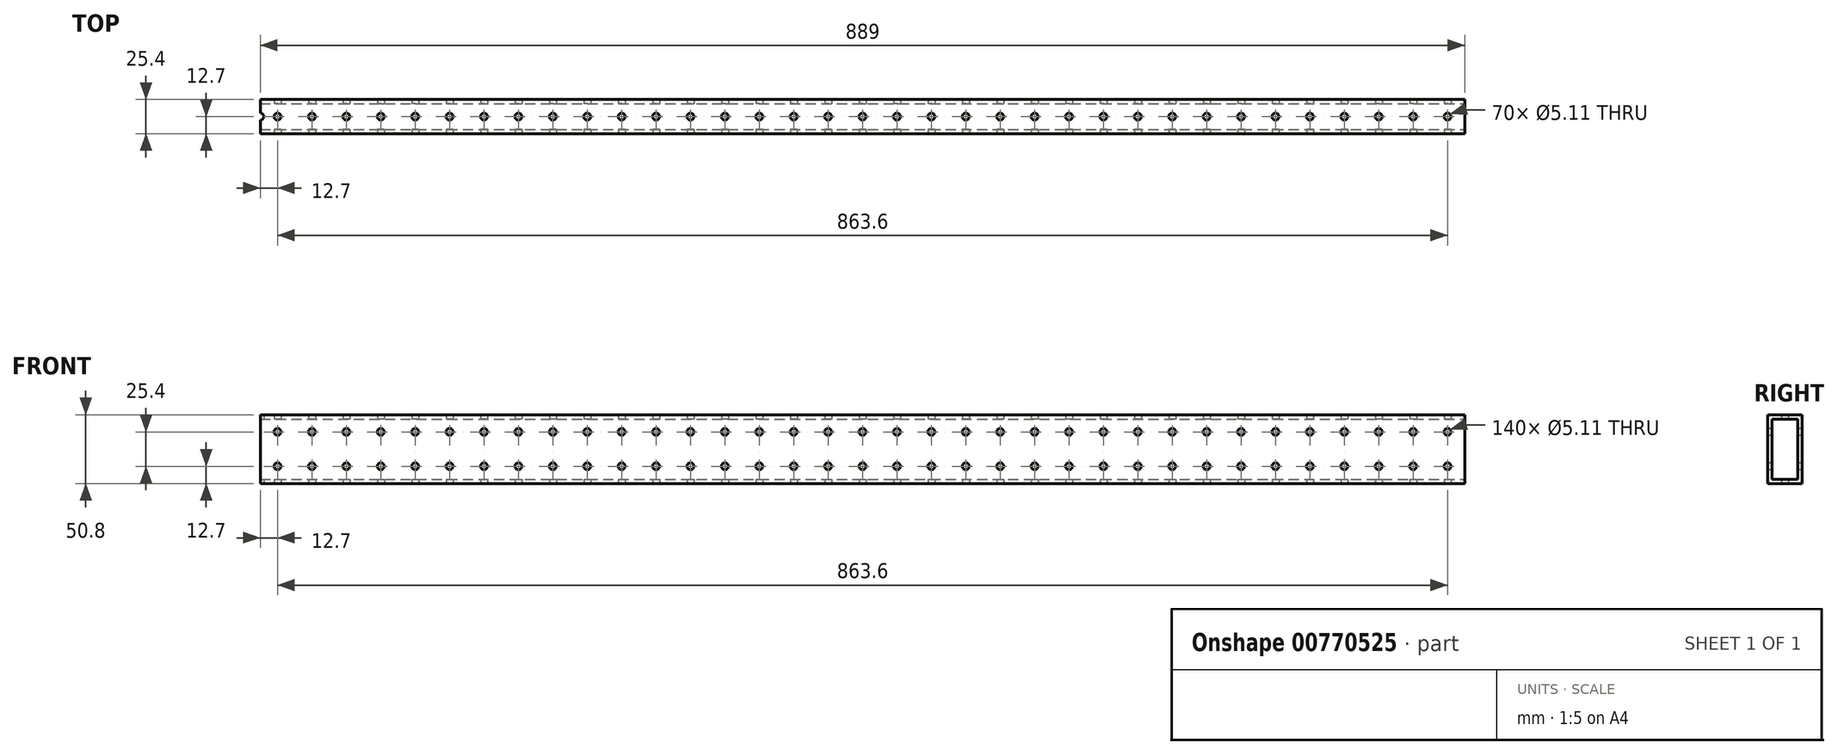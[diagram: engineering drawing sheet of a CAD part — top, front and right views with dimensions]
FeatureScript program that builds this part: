
annotation { "Feature Type Name" : "Feature", "Feature Type Description" : "" }
export const myFeature = defineFeature(function(context is Context, id is Id, definition is map)
    precondition{}
    {
        {
            var Q0;
            Q0=qCreatedBy(makeId("Front.planeOp"),FACE);
            var sketch = newSketch(context, id + "F0", { "sketchPlane" : qUnion([Q0])});
            skLineSegment(sketch, "E0.bottom", {"start": v(444.5, -25.4) * mm, "end": v(-444.5, -25.4) * mm});
            skLineSegment(sketch, "E0.top", {"start": v(444.5, 25.4) * mm, "end": v(-444.5, 25.4) * mm});
            skLineSegment(sketch, "E0.left", {"start": v(444.5, -25.4) * mm, "end": v(444.5, 25.4) * mm});
            skLineSegment(sketch, "E0.right", {"start": v(-444.5, -25.4) * mm, "end": v(-444.5, 25.4) * mm});
            skPoint(sketch, "E0.middle", {"position": v(0, 0) * mm});
            skSolve(sketch);
        }
        {
            var Q0;
            Q0=makeQuery(id+"F0.imprint","IMPRINT",FACE,{"disambiguationData":[TD([[makeQuery(id+"F0.imprint","IMPRINT",EDGE,{"derivedFrom":sQuery(id+"F0.wireOp",EDGE,"E0.bottom")}),-1.0]])]});
            extrude(context, id + "F1", {"entities" : qUnion([Q0]), "depth" : 25.4 * mm, "offsetDistance" : 25.4 * mm});
        }
        {
            var Q0;
            Q0=makeQuery(id+"F1.opExtrude","CAP_FACE",FACE,{"disambiguationData":[OSD([sQuery(id+"F0.wireOp",EDGE,"E0.bottom"),sQuery(id+"F0.wireOp",EDGE,"E0.top"),sQuery(id+"F0.wireOp",EDGE,"E0.left"),sQuery(id+"F0.wireOp",EDGE,"E0.right")])],"isStart":false});
            var sketch = newSketch(context, id + "F2", { "sketchPlane" : qUnion([Q0])});
            skCircle(sketch, "E1", {"center": v(-431.8, -12.7) * mm, "radius": 2.55 * mm});
            skCircle(sketch, "E2.0.1.0", {"center": v(-431.8, 12.7) * mm, "radius": 2.55 * mm});
            skCircle(sketch, "E2.1.0.0", {"center": v(-406.4, -12.7) * mm, "radius": 2.55 * mm});
            skCircle(sketch, "E2.1.1.0", {"center": v(-406.4, 12.7) * mm, "radius": 2.55 * mm});
            skCircle(sketch, "E2.2.0.0", {"center": v(-381, -12.7) * mm, "radius": 2.55 * mm});
            skCircle(sketch, "E2.2.1.0", {"center": v(-381, 12.7) * mm, "radius": 2.55 * mm});
            skCircle(sketch, "E2.3.0.0", {"center": v(-355.6, -12.7) * mm, "radius": 2.55 * mm});
            skCircle(sketch, "E2.3.1.0", {"center": v(-355.6, 12.7) * mm, "radius": 2.55 * mm});
            skCircle(sketch, "E2.4.0.0", {"center": v(-330.2, -12.7) * mm, "radius": 2.55 * mm});
            skCircle(sketch, "E2.4.1.0", {"center": v(-330.2, 12.7) * mm, "radius": 2.55 * mm});
            skCircle(sketch, "E2.5.0.0", {"center": v(-304.8, -12.7) * mm, "radius": 2.55 * mm});
            skCircle(sketch, "E2.5.1.0", {"center": v(-304.8, 12.7) * mm, "radius": 2.55 * mm});
            skCircle(sketch, "E2.6.0.0", {"center": v(-279.4, -12.7) * mm, "radius": 2.55 * mm});
            skCircle(sketch, "E2.6.1.0", {"center": v(-279.4, 12.7) * mm, "radius": 2.55 * mm});
            skCircle(sketch, "E2.7.0.0", {"center": v(-254, -12.7) * mm, "radius": 2.55 * mm});
            skCircle(sketch, "E2.7.1.0", {"center": v(-254, 12.7) * mm, "radius": 2.55 * mm});
            skCircle(sketch, "E2.8.0.0", {"center": v(-228.6, -12.7) * mm, "radius": 2.55 * mm});
            skCircle(sketch, "E2.8.1.0", {"center": v(-228.6, 12.7) * mm, "radius": 2.55 * mm});
            skCircle(sketch, "E2.9.0.0", {"center": v(-203.2, -12.7) * mm, "radius": 2.55 * mm});
            skCircle(sketch, "E2.9.1.0", {"center": v(-203.2, 12.7) * mm, "radius": 2.55 * mm});
            skCircle(sketch, "E2.10.0.0", {"center": v(-177.8, -12.7) * mm, "radius": 2.55 * mm});
            skCircle(sketch, "E2.10.1.0", {"center": v(-177.8, 12.7) * mm, "radius": 2.55 * mm});
            skCircle(sketch, "E2.11.0.0", {"center": v(-152.4, -12.7) * mm, "radius": 2.55 * mm});
            skCircle(sketch, "E2.11.1.0", {"center": v(-152.4, 12.7) * mm, "radius": 2.55 * mm});
            skCircle(sketch, "E2.12.0.0", {"center": v(-127, -12.7) * mm, "radius": 2.55 * mm});
            skCircle(sketch, "E2.12.1.0", {"center": v(-127, 12.7) * mm, "radius": 2.55 * mm});
            skCircle(sketch, "E2.13.0.0", {"center": v(-101.6, -12.7) * mm, "radius": 2.55 * mm});
            skCircle(sketch, "E2.13.1.0", {"center": v(-101.6, 12.7) * mm, "radius": 2.55 * mm});
            skCircle(sketch, "E2.14.0.0", {"center": v(-76.2, -12.7) * mm, "radius": 2.55 * mm});
            skCircle(sketch, "E2.14.1.0", {"center": v(-76.2, 12.7) * mm, "radius": 2.55 * mm});
            skCircle(sketch, "E2.15.0.0", {"center": v(-50.8, -12.7) * mm, "radius": 2.55 * mm});
            skCircle(sketch, "E2.15.1.0", {"center": v(-50.8, 12.7) * mm, "radius": 2.55 * mm});
            skCircle(sketch, "E2.16.0.0", {"center": v(-25.4, -12.7) * mm, "radius": 2.55 * mm});
            skCircle(sketch, "E2.16.1.0", {"center": v(-25.4, 12.7) * mm, "radius": 2.55 * mm});
            skCircle(sketch, "E2.17.0.0", {"center": v(0, -12.7) * mm, "radius": 2.55 * mm});
            skCircle(sketch, "E2.17.1.0", {"center": v(0, 12.7) * mm, "radius": 2.55 * mm});
            skCircle(sketch, "E2.18.0.0", {"center": v(25.4, -12.7) * mm, "radius": 2.55 * mm});
            skCircle(sketch, "E2.18.1.0", {"center": v(25.4, 12.7) * mm, "radius": 2.55 * mm});
            skCircle(sketch, "E2.19.0.0", {"center": v(50.8, -12.7) * mm, "radius": 2.55 * mm});
            skCircle(sketch, "E2.19.1.0", {"center": v(50.8, 12.7) * mm, "radius": 2.55 * mm});
            skCircle(sketch, "E2.20.0.0", {"center": v(76.2, -12.7) * mm, "radius": 2.55 * mm});
            skCircle(sketch, "E2.20.1.0", {"center": v(76.2, 12.7) * mm, "radius": 2.55 * mm});
            skCircle(sketch, "E2.21.0.0", {"center": v(101.6, -12.7) * mm, "radius": 2.55 * mm});
            skCircle(sketch, "E2.21.1.0", {"center": v(101.6, 12.7) * mm, "radius": 2.55 * mm});
            skCircle(sketch, "E2.22.0.0", {"center": v(127, -12.7) * mm, "radius": 2.55 * mm});
            skCircle(sketch, "E2.22.1.0", {"center": v(127, 12.7) * mm, "radius": 2.55 * mm});
            skCircle(sketch, "E2.23.0.0", {"center": v(152.4, -12.7) * mm, "radius": 2.55 * mm});
            skCircle(sketch, "E2.23.1.0", {"center": v(152.4, 12.7) * mm, "radius": 2.55 * mm});
            skCircle(sketch, "E2.24.0.0", {"center": v(177.8, -12.7) * mm, "radius": 2.55 * mm});
            skCircle(sketch, "E2.24.1.0", {"center": v(177.8, 12.7) * mm, "radius": 2.55 * mm});
            skCircle(sketch, "E2.25.0.0", {"center": v(203.2, -12.7) * mm, "radius": 2.55 * mm});
            skCircle(sketch, "E2.25.1.0", {"center": v(203.2, 12.7) * mm, "radius": 2.55 * mm});
            skCircle(sketch, "E2.26.0.0", {"center": v(228.6, -12.7) * mm, "radius": 2.55 * mm});
            skCircle(sketch, "E2.26.1.0", {"center": v(228.6, 12.7) * mm, "radius": 2.55 * mm});
            skCircle(sketch, "E2.27.0.0", {"center": v(254, -12.7) * mm, "radius": 2.55 * mm});
            skCircle(sketch, "E2.27.1.0", {"center": v(254, 12.7) * mm, "radius": 2.55 * mm});
            skCircle(sketch, "E2.28.0.0", {"center": v(279.4, -12.7) * mm, "radius": 2.55 * mm});
            skCircle(sketch, "E2.28.1.0", {"center": v(279.4, 12.7) * mm, "radius": 2.55 * mm});
            skCircle(sketch, "E2.29.0.0", {"center": v(304.8, -12.7) * mm, "radius": 2.55 * mm});
            skCircle(sketch, "E2.29.1.0", {"center": v(304.8, 12.7) * mm, "radius": 2.55 * mm});
            skCircle(sketch, "E2.30.0.0", {"center": v(330.2, -12.7) * mm, "radius": 2.55 * mm});
            skCircle(sketch, "E2.30.1.0", {"center": v(330.2, 12.7) * mm, "radius": 2.55 * mm});
            skCircle(sketch, "E2.31.0.0", {"center": v(355.6, -12.7) * mm, "radius": 2.55 * mm});
            skCircle(sketch, "E2.31.1.0", {"center": v(355.6, 12.7) * mm, "radius": 2.55 * mm});
            skCircle(sketch, "E2.32.0.0", {"center": v(381, -12.7) * mm, "radius": 2.55 * mm});
            skCircle(sketch, "E2.32.1.0", {"center": v(381, 12.7) * mm, "radius": 2.55 * mm});
            skCircle(sketch, "E2.33.0.0", {"center": v(406.4, -12.7) * mm, "radius": 2.55 * mm});
            skCircle(sketch, "E2.33.1.0", {"center": v(406.4, 12.7) * mm, "radius": 2.55 * mm});
            skCircle(sketch, "E2.34.0.0", {"center": v(431.8, -12.7) * mm, "radius": 2.55 * mm});
            skCircle(sketch, "E2.34.1.0", {"center": v(431.8, 12.7) * mm, "radius": 2.55 * mm});
            skLineSegment(sketch, "E2.direction1", {"start": v(-431.8, -12.7) * mm, "end": v(-406.4, -12.7) * mm, "construction": true});
            skLineSegment(sketch, "E2.direction2", {"start": v(-431.8, -12.7) * mm, "end": v(-431.8, 12.7) * mm, "construction": true});
            skSolve(sketch);
        }
        {
            var Q0;
            Q0=sQuery(id+"F2.wireOp",VERTEX,"E2.30.0.0.center");
            var Q1;
            Q1=sQuery(id+"F2.wireOp",VERTEX,"E2.14.0.0.center");
            var Q2;
            Q2=sQuery(id+"F2.wireOp",VERTEX,"E2.22.0.0.center");
            var Q3;
            Q3=sQuery(id+"F2.wireOp",VERTEX,"E2.25.1.0.center");
            var Q4;
            Q4=sQuery(id+"F2.wireOp",VERTEX,"E2.17.1.0.center");
            var Q5;
            Q5=sQuery(id+"F2.wireOp",VERTEX,"E2.9.1.0.center");
            var Q6;
            Q6=sQuery(id+"F2.wireOp",VERTEX,"E2.6.1.0.center");
            var Q7;
            Q7=sQuery(id+"F2.wireOp",VERTEX,"E2.30.1.0.center");
            var Q8;
            Q8=sQuery(id+"F2.wireOp",VERTEX,"E2.22.1.0.center");
            var Q9;
            Q9=sQuery(id+"F2.wireOp",VERTEX,"E2.14.1.0.center");
            var Q10;
            Q10=sQuery(id+"F2.wireOp",VERTEX,"E2.26.0.0.center");
            var Q11;
            Q11=sQuery(id+"F2.wireOp",VERTEX,"E2.18.0.0.center");
            var Q12;
            Q12=sQuery(id+"F2.wireOp",VERTEX,"E2.10.0.0.center");
            var Q13;
            Q13=sQuery(id+"F2.wireOp",VERTEX,"E2.34.0.0.center");
            var Q14;
            Q14=sQuery(id+"F2.wireOp",VERTEX,"E2.4.1.0.center");
            var Q15;
            Q15=sQuery(id+"F2.wireOp",VERTEX,"E2.7.0.0.center");
            var Q16;
            Q16=sQuery(id+"F2.wireOp",VERTEX,"E2.5.0.0.center");
            var Q17;
            Q17=sQuery(id+"F2.wireOp",VERTEX,"E2.5.1.0.center");
            var Q18;
            Q18=sQuery(id+"F2.wireOp",VERTEX,"E2.31.0.0.center");
            var Q19;
            Q19=sQuery(id+"F2.wireOp",VERTEX,"E2.23.0.0.center");
            var Q20;
            Q20=sQuery(id+"F2.wireOp",VERTEX,"E2.15.0.0.center");
            var Q21;
            Q21=sQuery(id+"F2.wireOp",VERTEX,"E1.center");
            var Q22;
            Q22=sQuery(id+"F2.wireOp",VERTEX,"E2.0.1.0.center");
            var Q23;
            Q23=sQuery(id+"F2.wireOp",VERTEX,"E2.1.0.0.center");
            var Q24;
            Q24=sQuery(id+"F2.wireOp",VERTEX,"E2.1.1.0.center");
            var Q25;
            Q25=sQuery(id+"F2.wireOp",VERTEX,"E2.2.0.0.center");
            var Q26;
            Q26=sQuery(id+"F2.wireOp",VERTEX,"E2.2.1.0.center");
            var Q27;
            Q27=sQuery(id+"F2.wireOp",VERTEX,"E2.3.0.0.center");
            var Q28;
            Q28=sQuery(id+"F2.wireOp",VERTEX,"E2.3.1.0.center");
            var Q29;
            Q29=sQuery(id+"F2.wireOp",VERTEX,"E2.4.0.0.center");
            var Q30;
            Q30=sQuery(id+"F2.wireOp",VERTEX,"E2.26.1.0.center");
            var Q31;
            Q31=sQuery(id+"F2.wireOp",VERTEX,"E2.18.1.0.center");
            var Q32;
            Q32=sQuery(id+"F2.wireOp",VERTEX,"E2.10.1.0.center");
            var Q33;
            Q33=sQuery(id+"F2.wireOp",VERTEX,"E2.33.1.0.center");
            var Q34;
            Q34=sQuery(id+"F2.wireOp",VERTEX,"E2.6.0.0.center");
            var Q35;
            Q35=sQuery(id+"F2.wireOp",VERTEX,"E2.13.1.0.center");
            var Q36;
            Q36=sQuery(id+"F2.wireOp",VERTEX,"E2.21.1.0.center");
            var Q37;
            Q37=sQuery(id+"F2.wireOp",VERTEX,"E2.25.0.0.center");
            var Q38;
            Q38=sQuery(id+"F2.wireOp",VERTEX,"E2.17.0.0.center");
            var Q39;
            Q39=sQuery(id+"F2.wireOp",VERTEX,"E2.33.0.0.center");
            var Q40;
            Q40=sQuery(id+"F2.wireOp",VERTEX,"E2.29.1.0.center");
            var Q41;
            Q41=sQuery(id+"F2.wireOp",VERTEX,"E2.9.0.0.center");
            var Q42;
            Q42=sQuery(id+"F2.wireOp",VERTEX,"E2.12.0.0.center");
            var Q43;
            Q43=sQuery(id+"F2.wireOp",VERTEX,"E2.20.0.0.center");
            var Q44;
            Q44=sQuery(id+"F2.wireOp",VERTEX,"E2.28.0.0.center");
            var Q45;
            Q45=sQuery(id+"F2.wireOp",VERTEX,"E2.16.1.0.center");
            var Q46;
            Q46=sQuery(id+"F2.wireOp",VERTEX,"E2.13.0.0.center");
            var Q47;
            Q47=sQuery(id+"F2.wireOp",VERTEX,"E2.24.1.0.center");
            var Q48;
            Q48=sQuery(id+"F2.wireOp",VERTEX,"E2.21.0.0.center");
            var Q49;
            Q49=sQuery(id+"F2.wireOp",VERTEX,"E2.29.0.0.center");
            var Q50;
            Q50=sQuery(id+"F2.wireOp",VERTEX,"E2.32.1.0.center");
            var Q51;
            Q51=sQuery(id+"F2.wireOp",VERTEX,"E2.8.1.0.center");
            var Q52;
            Q52=sQuery(id+"F2.wireOp",VERTEX,"E2.11.1.0.center");
            var Q53;
            Q53=sQuery(id+"F2.wireOp",VERTEX,"E2.19.1.0.center");
            var Q54;
            Q54=sQuery(id+"F2.wireOp",VERTEX,"E2.27.1.0.center");
            var Q55;
            Q55=sQuery(id+"F2.wireOp",VERTEX,"E2.34.1.0.center");
            var Q56;
            Q56=sQuery(id+"F2.wireOp",VERTEX,"E2.7.1.0.center");
            var Q57;
            Q57=sQuery(id+"F2.wireOp",VERTEX,"E2.31.1.0.center");
            var Q58;
            Q58=sQuery(id+"F2.wireOp",VERTEX,"E2.23.1.0.center");
            var Q59;
            Q59=sQuery(id+"F2.wireOp",VERTEX,"E2.15.1.0.center");
            var Q60;
            Q60=sQuery(id+"F2.wireOp",VERTEX,"E2.27.0.0.center");
            var Q61;
            Q61=sQuery(id+"F2.wireOp",VERTEX,"E2.19.0.0.center");
            var Q62;
            Q62=sQuery(id+"F2.wireOp",VERTEX,"E2.11.0.0.center");
            var Q63;
            Q63=sQuery(id+"F2.wireOp",VERTEX,"E2.8.0.0.center");
            var Q64;
            Q64=sQuery(id+"F2.wireOp",VERTEX,"E2.28.1.0.center");
            var Q65;
            Q65=sQuery(id+"F2.wireOp",VERTEX,"E2.32.0.0.center");
            var Q66;
            Q66=sQuery(id+"F2.wireOp",VERTEX,"E2.20.1.0.center");
            var Q67;
            Q67=sQuery(id+"F2.wireOp",VERTEX,"E2.24.0.0.center");
            var Q68;
            Q68=sQuery(id+"F2.wireOp",VERTEX,"E2.12.1.0.center");
            var Q69;
            Q69=sQuery(id+"F2.wireOp",VERTEX,"E2.16.0.0.center");
            var Q70;
            Q70=makeQuery(id+"F1.opExtrude","SWEPT_BODY",BODY,{"disambiguationData":[OSD([sQuery(id+"F0.wireOp",EDGE,"E0.bottom"),sQuery(id+"F0.wireOp",EDGE,"E0.top"),sQuery(id+"F0.wireOp",EDGE,"E0.left"),sQuery(id+"F0.wireOp",EDGE,"E0.right")])]});
            hole(context, id + "F3", {"style" : HoleStyle.SIMPLE, "endStyle" : HoleEndStyle.BLIND, "holeDiameter" : 5.1 * mm, "majorDiameter" : 6.35 * mm, "holeDepth" : 50.8 * mm, "isTappedThrough" : true, "tappedDepth" : 12.7 * mm, "tapClearance" : 3, "startFromSketch" : true, "locations" : qUnion([Q0, Q1, Q2, Q3, Q4, Q5, Q6, Q7, Q8, Q9, Q10, Q11, Q12, Q13, Q14, Q15, Q16, Q17, Q18, Q19, Q20, Q21, Q22, Q23, Q24, Q25, Q26, Q27, Q28, Q29, Q30, Q31, Q32, Q33, Q34, Q35, Q36, Q37, Q38, Q39, Q40, Q41, Q42, Q43, Q44, Q45, Q46, Q47, Q48, Q49, Q50, Q51, Q52, Q53, Q54, Q55, Q56, Q57, Q58, Q59, Q60, Q61, Q62, Q63, Q64, Q65, Q66, Q67, Q68, Q69]), "scope" : qUnion([Q70])});
        }
        {
            var Q0;
            Q0=makeQuery(id+"F1.opExtrude","SWEPT_FACE",FACE,{"disambiguationData":[OSD([sQuery(id+"F0.wireOp",EDGE,"E0.bottom")])]});
            var sketch = newSketch(context, id + "F4", { "sketchPlane" : qUnion([Q0])});
            skCircle(sketch, "E3", {"center": v(-431.8, 12.7) * mm, "radius": 2.55 * mm});
            skPoint(sketch, "E3.centerSnap0", {"position": v(-444.5, 12.7) * mm});
            skCircle(sketch, "E4.1.0.0", {"center": v(-406.4, 12.7) * mm, "radius": 2.55 * mm});
            skCircle(sketch, "E4.2.0.0", {"center": v(-381, 12.7) * mm, "radius": 2.55 * mm});
            skCircle(sketch, "E4.3.0.0", {"center": v(-355.6, 12.7) * mm, "radius": 2.55 * mm});
            skCircle(sketch, "E4.4.0.0", {"center": v(-330.2, 12.7) * mm, "radius": 2.55 * mm});
            skCircle(sketch, "E4.5.0.0", {"center": v(-304.8, 12.7) * mm, "radius": 2.55 * mm});
            skCircle(sketch, "E4.6.0.0", {"center": v(-279.4, 12.7) * mm, "radius": 2.55 * mm});
            skCircle(sketch, "E4.7.0.0", {"center": v(-254, 12.7) * mm, "radius": 2.55 * mm});
            skCircle(sketch, "E4.8.0.0", {"center": v(-228.6, 12.7) * mm, "radius": 2.55 * mm});
            skCircle(sketch, "E4.9.0.0", {"center": v(-203.2, 12.7) * mm, "radius": 2.55 * mm});
            skCircle(sketch, "E4.10.0.0", {"center": v(-177.8, 12.7) * mm, "radius": 2.55 * mm});
            skCircle(sketch, "E4.11.0.0", {"center": v(-152.4, 12.7) * mm, "radius": 2.55 * mm});
            skCircle(sketch, "E4.12.0.0", {"center": v(-127, 12.7) * mm, "radius": 2.55 * mm});
            skCircle(sketch, "E4.13.0.0", {"center": v(-101.6, 12.7) * mm, "radius": 2.55 * mm});
            skCircle(sketch, "E4.14.0.0", {"center": v(-76.2, 12.7) * mm, "radius": 2.55 * mm});
            skCircle(sketch, "E4.15.0.0", {"center": v(-50.8, 12.7) * mm, "radius": 2.55 * mm});
            skCircle(sketch, "E4.16.0.0", {"center": v(-25.4, 12.7) * mm, "radius": 2.55 * mm});
            skCircle(sketch, "E4.17.0.0", {"center": v(0, 12.7) * mm, "radius": 2.55 * mm});
            skCircle(sketch, "E4.18.0.0", {"center": v(25.4, 12.7) * mm, "radius": 2.55 * mm});
            skCircle(sketch, "E4.19.0.0", {"center": v(50.8, 12.7) * mm, "radius": 2.55 * mm});
            skCircle(sketch, "E4.20.0.0", {"center": v(76.2, 12.7) * mm, "radius": 2.55 * mm});
            skCircle(sketch, "E4.21.0.0", {"center": v(101.6, 12.7) * mm, "radius": 2.55 * mm});
            skCircle(sketch, "E4.22.0.0", {"center": v(127, 12.7) * mm, "radius": 2.55 * mm});
            skCircle(sketch, "E4.23.0.0", {"center": v(152.4, 12.7) * mm, "radius": 2.55 * mm});
            skCircle(sketch, "E4.24.0.0", {"center": v(177.8, 12.7) * mm, "radius": 2.55 * mm});
            skCircle(sketch, "E4.25.0.0", {"center": v(203.2, 12.7) * mm, "radius": 2.55 * mm});
            skCircle(sketch, "E4.26.0.0", {"center": v(228.6, 12.7) * mm, "radius": 2.55 * mm});
            skCircle(sketch, "E4.27.0.0", {"center": v(254, 12.7) * mm, "radius": 2.55 * mm});
            skCircle(sketch, "E4.28.0.0", {"center": v(279.4, 12.7) * mm, "radius": 2.55 * mm});
            skCircle(sketch, "E4.29.0.0", {"center": v(304.8, 12.7) * mm, "radius": 2.55 * mm});
            skCircle(sketch, "E4.30.0.0", {"center": v(330.2, 12.7) * mm, "radius": 2.55 * mm});
            skCircle(sketch, "E4.31.0.0", {"center": v(355.6, 12.7) * mm, "radius": 2.55 * mm});
            skCircle(sketch, "E4.32.0.0", {"center": v(381, 12.7) * mm, "radius": 2.55 * mm});
            skCircle(sketch, "E4.33.0.0", {"center": v(406.4, 12.7) * mm, "radius": 2.55 * mm});
            skCircle(sketch, "E4.34.0.0", {"center": v(431.8, 12.7) * mm, "radius": 2.55 * mm});
            skLineSegment(sketch, "E4.direction1", {"start": v(-431.8, 12.7) * mm, "end": v(-406.4, 12.7) * mm, "construction": true});
            skSolve(sketch);
        }
        {
            var Q0;
            Q0=sQuery(id+"F4.wireOp",VERTEX,"E4.26.0.0.center");
            var Q1;
            Q1=sQuery(id+"F4.wireOp",VERTEX,"E4.7.0.0.center");
            var Q2;
            Q2=sQuery(id+"F4.wireOp",VERTEX,"E4.33.0.0.center");
            var Q3;
            Q3=sQuery(id+"F4.wireOp",VERTEX,"E4.17.0.0.center");
            var Q4;
            Q4=sQuery(id+"F4.wireOp",VERTEX,"E4.6.0.0.center");
            var Q5;
            Q5=sQuery(id+"F4.wireOp",VERTEX,"E4.9.0.0.center");
            var Q6;
            Q6=sQuery(id+"F4.wireOp",VERTEX,"E4.29.0.0.center");
            var Q7;
            Q7=sQuery(id+"F4.wireOp",VERTEX,"E4.8.0.0.center");
            var Q8;
            Q8=sQuery(id+"F4.wireOp",VERTEX,"E4.13.0.0.center");
            var Q9;
            Q9=sQuery(id+"F4.wireOp",VERTEX,"E4.24.0.0.center");
            var Q10;
            Q10=sQuery(id+"F4.wireOp",VERTEX,"E4.16.0.0.center");
            var Q11;
            Q11=sQuery(id+"F4.wireOp",VERTEX,"E4.32.0.0.center");
            var Q12;
            Q12=sQuery(id+"F4.wireOp",VERTEX,"E4.23.0.0.center");
            var Q13;
            Q13=sQuery(id+"F4.wireOp",VERTEX,"E4.22.0.0.center");
            var Q14;
            Q14=sQuery(id+"F4.wireOp",VERTEX,"E4.28.0.0.center");
            var Q15;
            Q15=sQuery(id+"F4.wireOp",VERTEX,"E4.19.0.0.center");
            var Q16;
            Q16=sQuery(id+"F4.wireOp",VERTEX,"E4.31.0.0.center");
            var Q17;
            Q17=sQuery(id+"F4.wireOp",VERTEX,"E4.15.0.0.center");
            var Q18;
            Q18=sQuery(id+"F4.wireOp",VERTEX,"E4.21.0.0.center");
            var Q19;
            Q19=sQuery(id+"F4.wireOp",VERTEX,"E4.18.0.0.center");
            var Q20;
            Q20=sQuery(id+"F4.wireOp",VERTEX,"E4.34.0.0.center");
            var Q21;
            Q21=sQuery(id+"F4.wireOp",VERTEX,"E4.27.0.0.center");
            var Q22;
            Q22=sQuery(id+"F4.wireOp",VERTEX,"E4.14.0.0.center");
            var Q23;
            Q23=sQuery(id+"F4.wireOp",VERTEX,"E4.30.0.0.center");
            var Q24;
            Q24=sQuery(id+"F4.wireOp",VERTEX,"E4.25.0.0.center");
            var Q25;
            Q25=sQuery(id+"F4.wireOp",VERTEX,"E3.centerSnap0");
            var Q26;
            Q26=sQuery(id+"F4.wireOp",VERTEX,"E4.direction1.start");
            var Q27;
            Q27=sQuery(id+"F4.wireOp",VERTEX,"E4.2.0.0.center");
            var Q28;
            Q28=sQuery(id+"F4.wireOp",VERTEX,"E4.20.0.0.center");
            var Q29;
            Q29=sQuery(id+"F4.wireOp",VERTEX,"E4.3.0.0.center");
            var Q30;
            Q30=sQuery(id+"F4.wireOp",VERTEX,"E4.5.0.0.center");
            var Q31;
            Q31=sQuery(id+"F4.wireOp",VERTEX,"E4.4.0.0.center");
            var Q32;
            Q32=sQuery(id+"F4.wireOp",VERTEX,"E4.10.0.0.center");
            var Q33;
            Q33=sQuery(id+"F4.wireOp",VERTEX,"E4.12.0.0.center");
            var Q34;
            Q34=sQuery(id+"F4.wireOp",VERTEX,"E4.11.0.0.center");
            var Q35;
            Q35=sQuery(id+"F4.wireOp",VERTEX,"E4.direction1.end");
            var Q36;
            Q36=makeQuery(id+"F1.opExtrude","SWEPT_BODY",BODY,{"disambiguationData":[OSD([sQuery(id+"F0.wireOp",EDGE,"E0.bottom"),sQuery(id+"F0.wireOp",EDGE,"E0.top"),sQuery(id+"F0.wireOp",EDGE,"E0.left"),sQuery(id+"F0.wireOp",EDGE,"E0.right")])]});
            hole(context, id + "F5", {"style" : HoleStyle.SIMPLE, "endStyle" : HoleEndStyle.BLIND, "holeDiameter" : 5.1 * mm, "majorDiameter" : 6.35 * mm, "holeDepth" : 50.8 * mm, "isTappedThrough" : true, "tappedDepth" : 12.7 * mm, "tapClearance" : 3, "startFromSketch" : true, "locations" : qUnion([Q0, Q1, Q2, Q3, Q4, Q5, Q6, Q7, Q8, Q9, Q10, Q11, Q12, Q13, Q14, Q15, Q16, Q17, Q18, Q19, Q20, Q21, Q22, Q23, Q24, Q25, Q26, Q27, Q28, Q29, Q30, Q31, Q32, Q33, Q34, Q35]), "scope" : qUnion([Q36])});
        }
        {
            var Q0;
            Q0=makeQuery(id+"F1.opExtrude","SWEPT_FACE",FACE,{"disambiguationData":[OSD([sQuery(id+"F0.wireOp",EDGE,"E0.left")])]});
            var sketch = newSketch(context, id + "F6", { "sketchPlane" : qUnion([Q0])});
            skLineSegment(sketch, "E5.0", {"start": v(-3.18, -22.23) * mm, "end": v(-3.18, 22.23) * mm});
            skLineSegment(sketch, "E5.1", {"start": v(-22.23, -22.23) * mm, "end": v(-3.18, -22.23) * mm});
            skLineSegment(sketch, "E5.2", {"start": v(-22.23, 22.23) * mm, "end": v(-22.23, -22.23) * mm});
            skLineSegment(sketch, "E5.3", {"start": v(-3.18, 22.23) * mm, "end": v(-22.23, 22.23) * mm});
            skSolve(sketch);
        }
        {
            var Q0;
            Q0=makeQuery(id+"F6.imprint","IMPRINT",FACE,{"disambiguationData":[TD([[makeQuery(id+"F6.imprint","IMPRINT",EDGE,{"derivedFrom":sQuery(id+"F6.wireOp",EDGE,"E5.0")}),1.0]])]});
            extrude(context, id + "F7", {"entities" : qUnion([Q0]), "operationType" : NewBodyOperationType.REMOVE, "oppositeDirection" : true, "depth" : 889 * mm, "offsetDistance" : 25.4 * mm});
        }
    });
